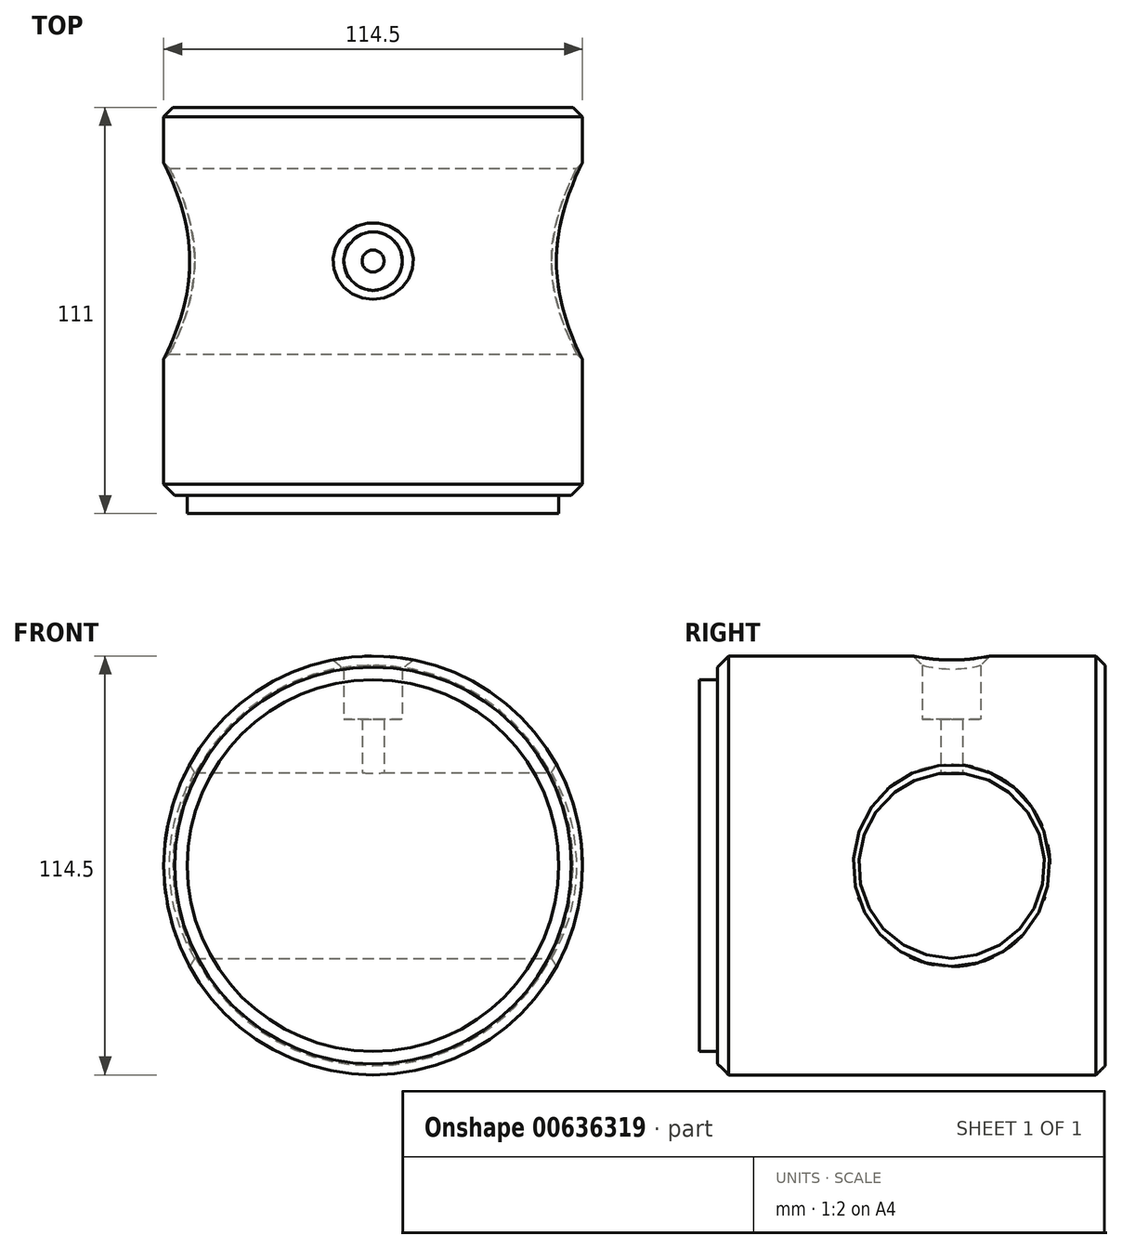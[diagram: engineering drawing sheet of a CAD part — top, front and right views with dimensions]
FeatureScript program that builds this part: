
annotation { "Feature Type Name" : "Feature", "Feature Type Description" : "" }
export const myFeature = defineFeature(function(context is Context, id is Id, definition is map)
    precondition{}
    {
        {
            var Q0;
            Q0=qCreatedBy(makeId("Front.planeOp"),FACE);
            var sketch = newSketch(context, id + "F0", { "sketchPlane" : qUnion([Q0])});
            skCircle(sketch, "E0", {"center": v(0, 0) * mm, "radius": 57.25 * mm});
            skSolve(sketch);
        }
        {
            var Q0;
            Q0=makeQuery(id+"F0.imprint","IMPRINT",FACE,{"disambiguationData":[TD([[makeQuery(id+"F0.imprint","IMPRINT",EDGE,{"derivedFrom":sQuery(id+"F0.wireOp",EDGE,"E0")}),1.0]])]});
            extrude(context, id + "F1", {"entities" : qUnion([Q0]), "depth" : 106 * mm, "offsetDistance" : 25 * mm});
        }
        {
            var Q0;
            Q0=makeQuery(id+"F1.opExtrude","CAP_FACE",FACE,{"disambiguationData":[OSD([sQuery(id+"F0.wireOp",EDGE,"E0")])],"isStart":false});
            var sketch = newSketch(context, id + "F2", { "sketchPlane" : qUnion([Q0])});
            skCircle(sketch, "E1", {"center": v(0, 0) * mm, "radius": 50.8 * mm});
            skSolve(sketch);
        }
        {
            var Q0;
            Q0=makeQuery(id+"F2.imprint","IMPRINT",FACE,{"disambiguationData":[TD([[makeQuery(id+"F2.imprint","IMPRINT",EDGE,{"derivedFrom":sQuery(id+"F2.wireOp",EDGE,"E1")}),1.0]])]});
            extrude(context, id + "F3", {"entities" : qUnion([Q0]), "operationType" : NewBodyOperationType.ADD, "depth" : 5 * mm, "offsetDistance" : 25 * mm});
        }
        {
            var Q0;
            Q0=makeQuery(id+"F1.opExtrude","CAP_EDGE",EDGE,{"disambiguationData":[OSD([sQuery(id+"F0.wireOp",EDGE,"E0")])],"isStart":false});
            chamfer(context, id + "F4", {"entities" : qUnion([Q0]), "width" : 3 * mm, "tangentPropagation" : true});
        }
        {
            var Q0;
            Q0=makeQuery(id+"F1.opExtrude","CAP_EDGE",EDGE,{"disambiguationData":[OSD([sQuery(id+"F0.wireOp",EDGE,"E0")])],"isStart":true});
            chamfer(context, id + "F5", {"entities" : qUnion([Q0]), "width" : 2.5 * mm, "tangentPropagation" : true});
        }
        {
            var Q0;
            Q0=qCreatedBy(makeId("Right.planeOp"),FACE);
            var sketch = newSketch(context, id + "F6", { "sketchPlane" : qUnion([Q0]), "disableImprinting" : false});
            skCircle(sketch, "E2", {"center": v(-42, 0) * mm, "radius": 25.4 * mm});
            skLineSegment(sketch, "E3", {"start": v(-42, 0) * mm, "end": v(0, 0) * mm, "construction": true});
            skLineSegment(sketch, "E4", {"start": v(-42, 0) * mm, "end": v(-42, 25.4) * mm, "construction": true});
            skLineSegment(sketch, "E5", {"start": v(-42, 0) * mm, "end": v(-42, -25.4) * mm, "construction": true});
            skSolve(sketch);
        }
        {
            var Q0;
            Q0 = qSketchRegion(id + "F6", true);
            var Q1;
            Q1=makeQuery(id+"F1.opExtrude","SWEPT_FACE",FACE,{"disambiguationData":[OSD([sQuery(id+"F0.wireOp",EDGE,"E0")])]});
            extrude(context, id + "F7", {"entities" : qUnion([Q0]), "operationType" : NewBodyOperationType.REMOVE, "oppositeDirection" : true, "depth" : 60 * mm, "endBoundEntityFace" : qUnion([Q1]), "offsetDistance" : 25 * mm, "hasSecondDirection" : true, "secondDirectionOppositeDirection" : false, "secondDirectionDepth" : 60 * mm});
        }
        {
            var Q0;
            Q0=qCreatedBy(makeId("Top.planeOp"),FACE);
            var sketch = newSketch(context, id + "F8", { "sketchPlane" : qUnion([Q0])});
            skCircle(sketch, "E6", {"center": v(0, -42) * mm, "radius": 3 * mm});
            skCircle(sketch, "E7", {"center": v(0, -42) * mm, "radius": 8 * mm});
            skSolve(sketch);
        }
        {
            var Q0;
            Q0=makeQuery(id+"F8.imprint","IMPRINT",FACE,{"disambiguationData":[TD([[makeQuery(id+"F8.imprint","IMPRINT",EDGE,{"derivedFrom":sQuery(id+"F8.wireOp",EDGE,"E6")}),1.0]])]});
            var Q1;
            Q1=makeQuery(id+"F1.opExtrude","SWEPT_FACE",FACE,{"disambiguationData":[OSD([sQuery(id+"F0.wireOp",EDGE,"E0")])]});
            extrude(context, id + "F9", {"entities" : qUnion([Q0]), "operationType" : NewBodyOperationType.REMOVE, "endBound" : BoundingType.UP_TO_SURFACE, "depth" : 25 * mm, "endBoundEntityFace" : qUnion([Q1]), "offsetDistance" : 25 * mm});
        }
        {
            var Q0;
            Q0 = qSketchRegion(id + "F8", true);
            extrude(context, id + "F10", {"entities" : qUnion([Q0]), "operationType" : NewBodyOperationType.REMOVE, "depth" : 60 * mm, "offsetDistance" : 25 * mm, "hasSecondDirection" : true, "secondDirectionOppositeDirection" : true, "secondDirectionDepth" : -40 * mm});
        }
        {
            var Q0;
            Q0=makeQuery(id+"F7.boolean.opBoolean","INTERSECT",EDGE,{"disambiguationData":[OD(0.0)],"derivedFrom":[makeQuery(id+"F1.opExtrude","SWEPT_FACE",FACE,{"disambiguationData":[OSD([sQuery(id+"F0.wireOp",EDGE,"E0")])]}),makeQuery(id+"F7.opExtrude","SWEPT_FACE",FACE,{"disambiguationData":[OSD([sQuery(id+"F6.wireOp",EDGE,"E2")])]})]});
            var Q1;
            Q1=makeQuery(id+"F10.boolean.opBoolean","INTERSECT",EDGE,{"derivedFrom":[makeQuery(id+"F1.opExtrude","SWEPT_FACE",FACE,{"disambiguationData":[OSD([sQuery(id+"F0.wireOp",EDGE,"E0")])]}),makeQuery(id+"F10.opExtrude","SWEPT_FACE",FACE,{"disambiguationData":[OSD([sQuery(id+"F8.wireOp",EDGE,"E7")])]})]});
            var Q2;
            Q2=makeQuery(id+"F7.boolean.opBoolean","INTERSECT",EDGE,{"disambiguationData":[OD(1.0)],"derivedFrom":[makeQuery(id+"F1.opExtrude","SWEPT_FACE",FACE,{"disambiguationData":[OSD([sQuery(id+"F0.wireOp",EDGE,"E0")])]}),makeQuery(id+"F7.opExtrude","SWEPT_FACE",FACE,{"disambiguationData":[OSD([sQuery(id+"F6.wireOp",EDGE,"E2")])]})]});
            chamfer(context, id + "F11", {"entities" : qUnion([Q0, Q1, Q2]), "width" : 2.5 * mm, "tangentPropagation" : true});
        }
    });
